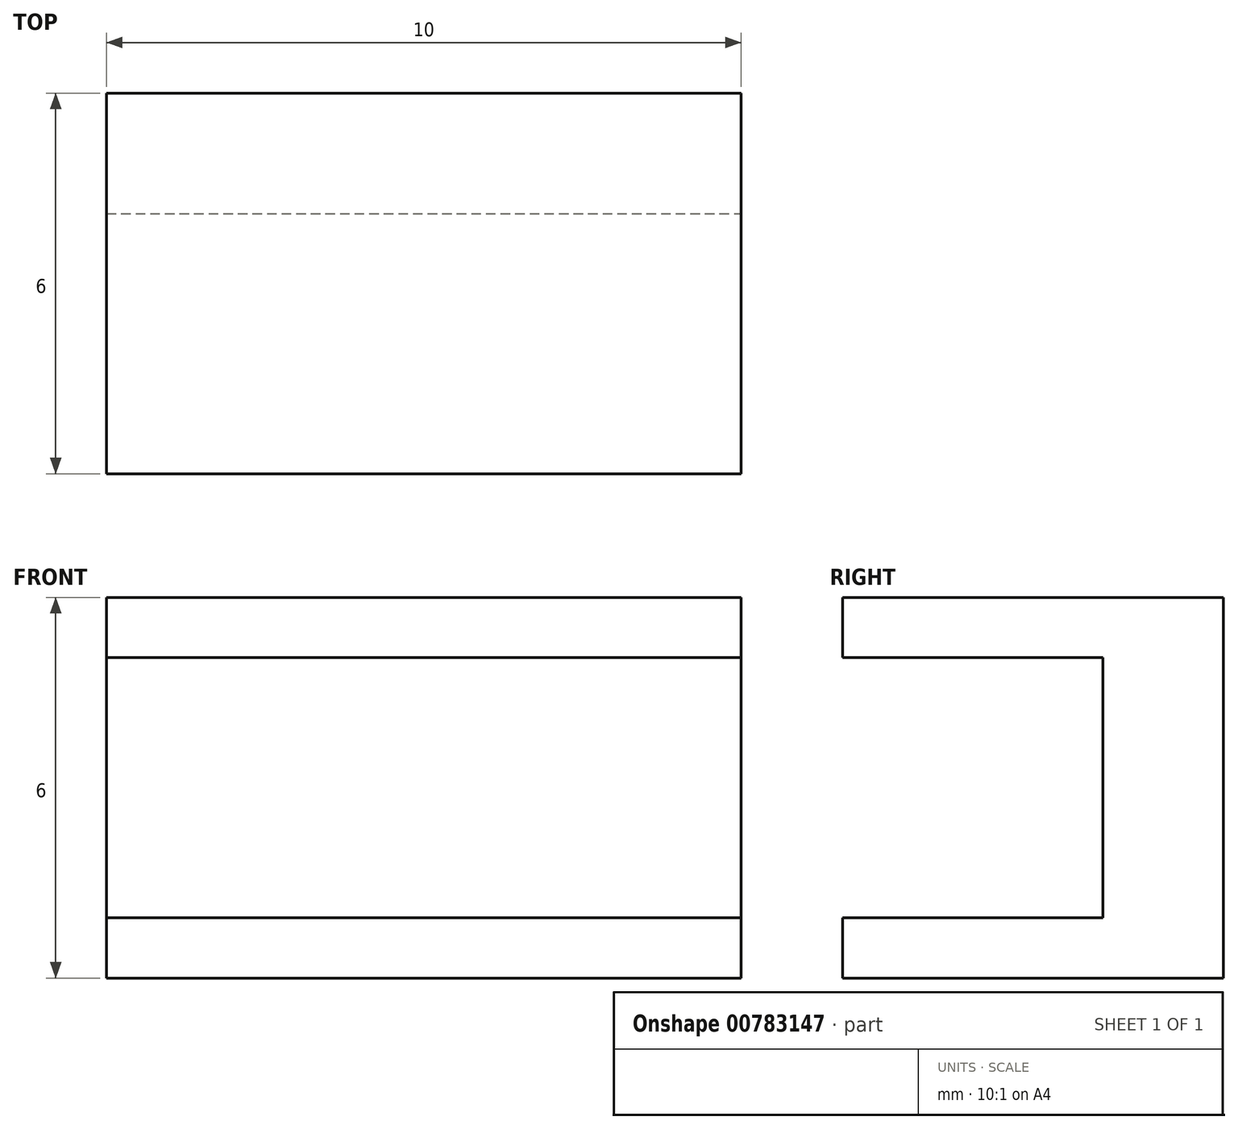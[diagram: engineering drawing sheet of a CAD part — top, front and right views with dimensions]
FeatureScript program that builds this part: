
annotation { "Feature Type Name" : "Feature", "Feature Type Description" : "" }
export const myFeature = defineFeature(function(context is Context, id is Id, definition is map)
    precondition{}
    {
        {
            var Q0;
            Q0=qCreatedBy(makeId("Top.planeOp"),FACE);
            var sketch = newSketch(context, id + "F0", { "sketchPlane" : qUnion([Q0])});
            skLineSegment(sketch, "E0.bottom", {"start": v(0, 0) * mm, "end": v(10, 0) * mm});
            skLineSegment(sketch, "E0.top", {"start": v(0, 6) * mm, "end": v(10, 6) * mm});
            skLineSegment(sketch, "E0.left", {"start": v(0, 0) * mm, "end": v(0, 6) * mm});
            skLineSegment(sketch, "E0.right", {"start": v(10, 0) * mm, "end": v(10, 6) * mm});
            skSolve(sketch);
        }
        {
            var Q0;
            Q0=makeQuery(id+"F0.imprint","IMPRINT",FACE,{"disambiguationData":[TD([[makeQuery(id+"F0.imprint","IMPRINT",EDGE,{"derivedFrom":sQuery(id+"F0.wireOp",EDGE,"E0.bottom")}),1.0]])]});
            extrude(context, id + "F1", {"entities" : qUnion([Q0]), "depth" : 6 * mm, "offsetDistance" : 25 * mm});
        }
        {
            var Q0;
            Q0=makeQuery(id+"F1.opExtrude","SWEPT_FACE",FACE,{"disambiguationData":[OSD([sQuery(id+"F0.wireOp",EDGE,"E0.right")])]});
            var sketch = newSketch(context, id + "F2", { "sketchPlane" : qUnion([Q0])});
            skLineSegment(sketch, "E1.bottom", {"start": v(0, 5.05) * mm, "end": v(4.1, 5.05) * mm});
            skLineSegment(sketch, "E1.top", {"start": v(0, 0.95) * mm, "end": v(4.1, 0.95) * mm});
            skLineSegment(sketch, "E1.left", {"start": v(0, 5.05) * mm, "end": v(0, 0.95) * mm});
            skLineSegment(sketch, "E1.right", {"start": v(4.1, 5.05) * mm, "end": v(4.1, 0.95) * mm});
            skLineSegment(sketch, "E2", {"start": v(6, 3) * mm, "end": v(0, 3) * mm, "construction": true});
            skLineSegment(sketch, "E3", {"start": v(4.1, 3) * mm, "end": v(0, 3) * mm, "construction": true});
            skSolve(sketch);
        }
        {
            var Q0;
            Q0=makeQuery(id+"F2.imprint","IMPRINT",FACE,{"disambiguationData":[TD([[makeQuery(id+"F2.imprint","IMPRINT",EDGE,{"derivedFrom":sQuery(id+"F2.wireOp",EDGE,"E1.bottom")}),-1.0]])]});
            extrude(context, id + "F3", {"entities" : qUnion([Q0]), "operationType" : NewBodyOperationType.REMOVE, "endBound" : BoundingType.UP_TO_NEXT, "oppositeDirection" : true, "depth" : 25 * mm, "offsetDistance" : 25 * mm});
        }
    });
